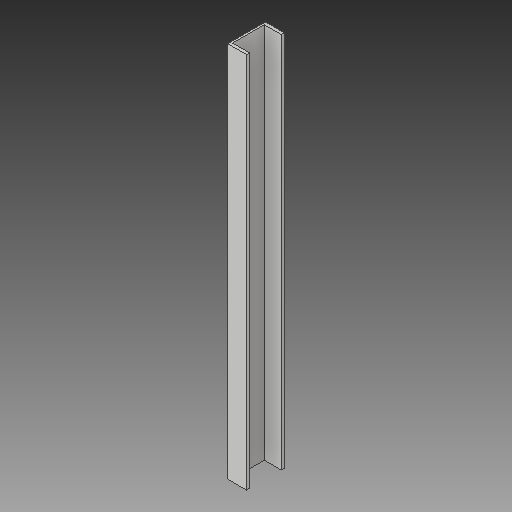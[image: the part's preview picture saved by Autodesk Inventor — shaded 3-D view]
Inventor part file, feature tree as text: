
AUTODESK INVENTOR PART (.ipt)
format: ipt  version: 2019 (Build 230136000, 136)  size: 86,528 bytes
history: native  units: in
note: dims shown in document units (in); Inventor stores cm internally (conversion verified against a paired STEP export)
features: other x3, sketch x1
ambient origin geometry x8: Origin, YZ Plane, XZ Plane, XY Plane, X Axis, Y Axis, Z Axis, Center Point
bodies: Solid1 (feature_tree)
feature tree (4):
  other  "Channel1_MIR_MIR_MIR.ipt"
  other  "Solid1::Channel1_MIR_MIR_MIR.ipt"
  other  "TaggingFeature1"
  sketch  "Sketch1"  dims[d0=0.3937in]
